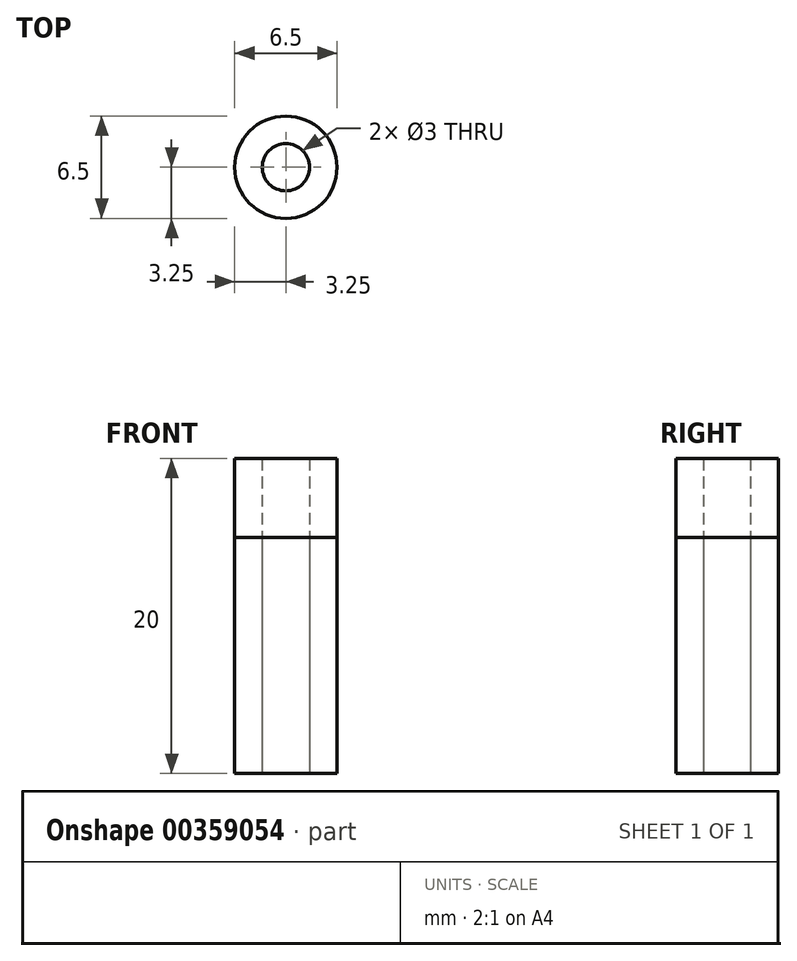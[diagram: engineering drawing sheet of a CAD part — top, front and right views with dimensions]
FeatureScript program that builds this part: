
annotation { "Feature Type Name" : "Feature", "Feature Type Description" : "" }
export const myFeature = defineFeature(function(context is Context, id is Id, definition is map)
    precondition{}
    {
        {
            var Q0;
            Q0=qCreatedBy(makeId("Top.planeOp"),FACE);
            var sketch = newSketch(context, id + "F0", { "sketchPlane" : qUnion([Q0])});
            skCircle(sketch, "E0", {"center": v(0, 0) * mm, "radius": 3.25 * mm});
            skCircle(sketch, "E1", {"center": v(0, 0) * mm, "radius": 1.5 * mm});
            skSolve(sketch);
        }
        {
            var Q0;
            Q0 = qSketchRegion(id + "F0", true);
            extrude(context, id + "F1", {"entities" : qUnion([Q0]), "depth" : 15 * mm, "offsetDistance" : 25 * mm});
        }
        {
            var Q0;
            Q0 = qSketchRegion(id + "F0", true);
            extrude(context, id + "F2", {"entities" : qUnion([Q0]), "depth" : 20 * mm, "offsetDistance" : 25 * mm});
        }
    });
